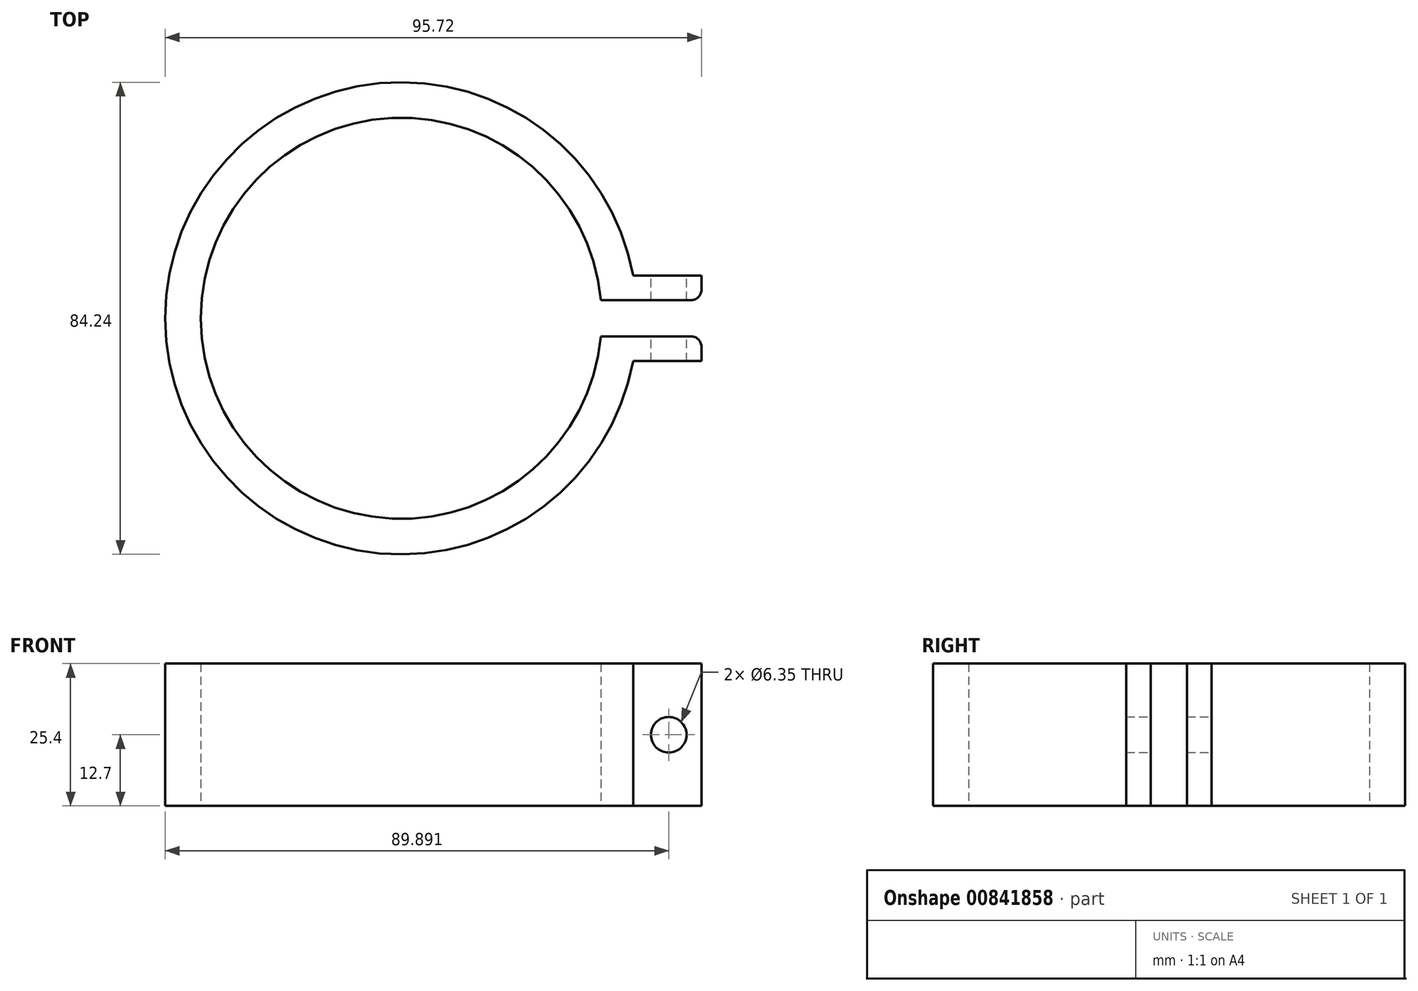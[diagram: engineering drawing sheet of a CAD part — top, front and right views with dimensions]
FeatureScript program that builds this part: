
annotation { "Feature Type Name" : "Feature", "Feature Type Description" : "" }
export const myFeature = defineFeature(function(context is Context, id is Id, definition is map)
    precondition{}
    {
        {
            var Q0;
            Q0=qCreatedBy(makeId("Top.planeOp"),FACE);
            var sketch = newSketch(context, id + "F0", { "sketchPlane" : qUnion([Q0])});
            skArc(sketch, "E0", {"start": v(35.63, 3.24) * mm, "mid": v(-35.77, 0) * mm, "end": v(35.63, -3.24) * mm});
            skLineSegment(sketch, "E1", {"start": v(35.63, 3.24) * mm, "end": v(53.6, 3.24) * mm});
            skLineSegment(sketch, "E2", {"start": v(53.6, 3.24) * mm, "end": v(53.6, 7.63) * mm});
            skLineSegment(sketch, "E3", {"start": v(53.6, 7.63) * mm, "end": v(34.95, 7.63) * mm});
            skLineSegment(sketch, "E4.MirrorCS", {"start": v(35.63, -3.24) * mm, "end": v(53.6, -3.24) * mm});
            skLineSegment(sketch, "E5.MirrorCS", {"start": v(53.6, -7.63) * mm, "end": v(34.95, -7.63) * mm});
            skLineSegment(sketch, "E6.MirrorCS", {"start": v(53.6, -3.24) * mm, "end": v(53.6, -7.63) * mm});
            skArc(sketch, "E7.0", {"start": v(42, 3.24) * mm, "mid": v(-42.12, 0) * mm, "end": v(42, -3.24) * mm});
            skSolve(sketch);
        }
        {
            var Q0;
            Q0 = qSketchRegion(id + "F0", true);
            extrude(context, id + "F1", {"entities" : qUnion([Q0]), "depth" : 25.4 * mm, "offsetDistance" : 25.4 * mm});
        }
        {
            var Q0;
            Q0=makeQuery(id+"F1.opExtrude","SWEPT_FACE",FACE,{"disambiguationData":[OSD([sQuery(id+"F0.wireOp",EDGE,"E3")])]});
            var sketch = newSketch(context, id + "F2", { "sketchPlane" : qUnion([Q0])});
            skPoint(sketch, "E8", {"position": v(-47.77, 12.7) * mm});
            skPoint(sketch, "E8.positionSnap0", {"position": v(-53.6, 12.7) * mm});
            skSolve(sketch);
        }
        {
            var Q0;
            Q0=sQuery(id+"F2.wireOp",VERTEX,"E8");
            var Q1;
            Q1=makeQuery(id+"F1.opExtrude","SWEPT_BODY",BODY,{"disambiguationData":[OSD([sQuery(id+"F0.wireOp",EDGE,"E0"),sQuery(id+"F0.wireOp",EDGE,"E1"),sQuery(id+"F0.wireOp",EDGE,"E2"),sQuery(id+"F0.wireOp",EDGE,"E3"),sQuery(id+"F0.wireOp",EDGE,"E4.MirrorCS"),sQuery(id+"F0.wireOp",EDGE,"E5.MirrorCS"),sQuery(id+"F0.wireOp",EDGE,"E6.MirrorCS"),sQuery(id+"F0.wireOp",EDGE,"E7.0")])]});
            hole(context, id + "F3", {"style" : HoleStyle.SIMPLE, "endStyle" : HoleEndStyle.THROUGH, "holeDiameter" : 6.35 * mm, "majorDiameter" : 6.35 * mm, "isTappedThrough" : true, "tappedDepth" : 12.7 * mm, "tapClearance" : 3, "locations" : qUnion([Q0]), "scope" : qUnion([Q1])});
        }
        {
            var Q0;
            Q0=makeQuery(id+"F1.opExtrude","SWEPT_EDGE",EDGE,{"disambiguationData":[OSD([sQuery(id+"F0.wireOp",EDGE,"E1"),sQuery(id+"F0.wireOp",EDGE,"E2")])]});
            var Q1;
            Q1=makeQuery(id+"F1.opExtrude","SWEPT_EDGE",EDGE,{"disambiguationData":[OSD([sQuery(id+"F0.wireOp",EDGE,"E4.MirrorCS"),sQuery(id+"F0.wireOp",EDGE,"E6.MirrorCS")])]});
            fillet(context, id + "F4", {"entities" : qUnion([Q0, Q1]), "radius" : 1.84 * mm, "tangentPropagation" : true, "allowEdgeOverflow" : false});
        }
    });
